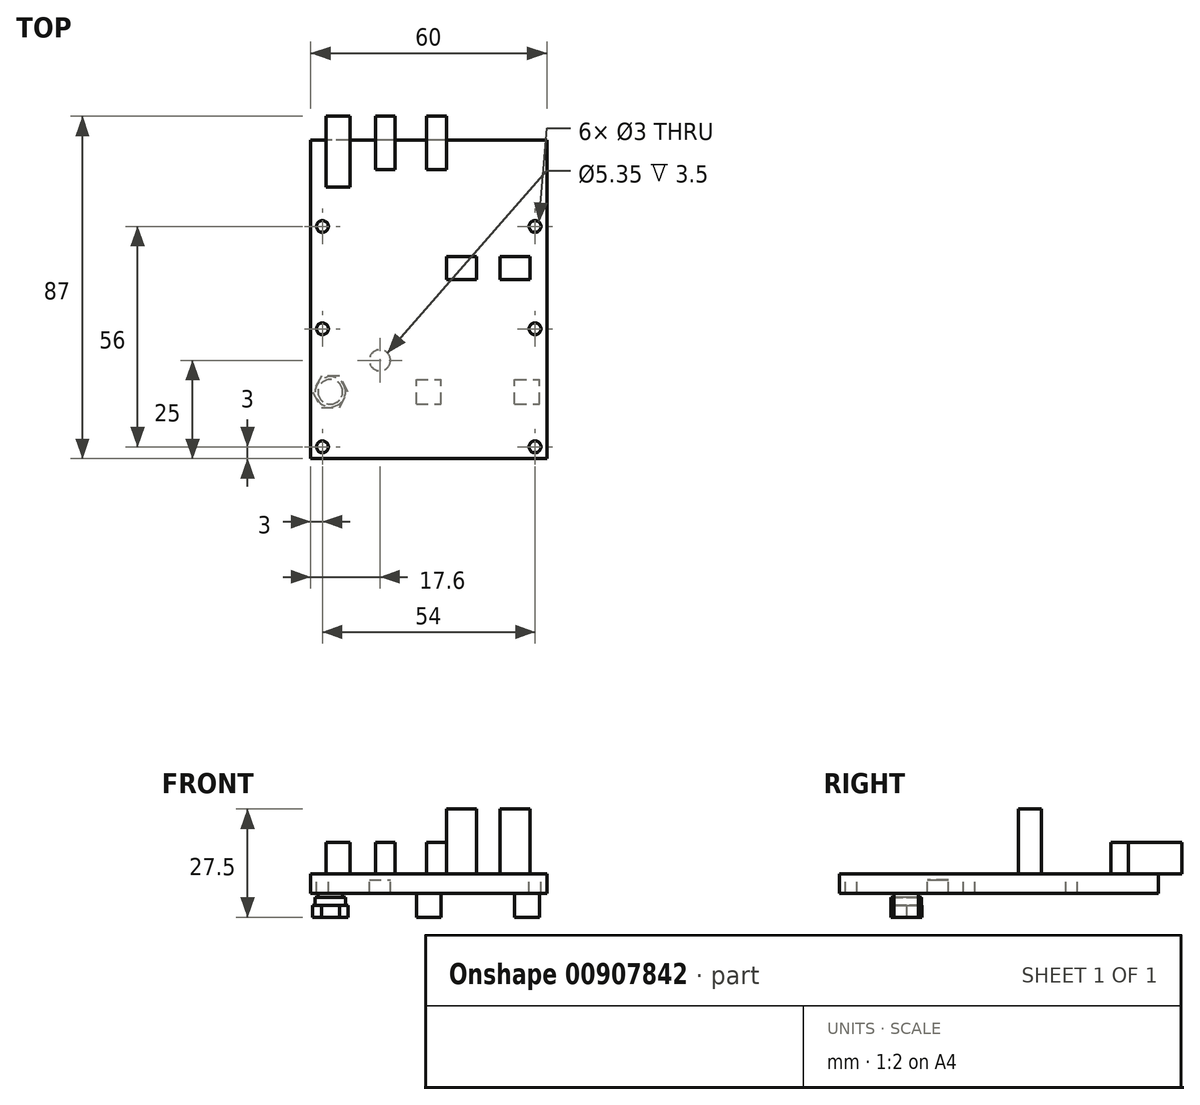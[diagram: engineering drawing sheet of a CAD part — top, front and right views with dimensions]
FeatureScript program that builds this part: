
annotation { "Feature Type Name" : "Feature", "Feature Type Description" : "" }
export const myFeature = defineFeature(function(context is Context, id is Id, definition is map)
    precondition{}
    {
        {
            var Q0;
            Q0=qCreatedBy(makeId("Top.planeOp"),FACE);
            var sketch = newSketch(context, id + "F0", { "sketchPlane" : qUnion([Q0])});
            skLineSegment(sketch, "E0.bottom", {"start": v(30, 40.5) * mm, "end": v(-30, 40.5) * mm});
            skLineSegment(sketch, "E0.top", {"start": v(30, -40.5) * mm, "end": v(-30, -40.5) * mm});
            skLineSegment(sketch, "E0.left", {"start": v(30, 40.5) * mm, "end": v(30, -40.5) * mm});
            skLineSegment(sketch, "E0.right", {"start": v(-30, 40.5) * mm, "end": v(-30, -40.5) * mm});
            skPoint(sketch, "E0.middle", {"position": v(0, 0) * mm});
            skSolve(sketch);
        }
        {
            var Q0;
            Q0=makeQuery(id+"F0.imprint","IMPRINT",FACE,{"disambiguationData":[TD([[makeQuery(id+"F0.imprint","IMPRINT",EDGE,{"derivedFrom":sQuery(id+"F0.wireOp",EDGE,"E0.bottom")}),1.0]])]});
            extrude(context, id + "F1", {"entities" : qUnion([Q0]), "depth" : 1.5 * mm, "offsetDistance" : 25 * mm});
        }
        {
            var Q0;
            Q0=makeQuery(id+"F1.opExtrude","CAP_FACE",FACE,{"disambiguationData":[OSD([sQuery(id+"F0.wireOp",EDGE,"E0.bottom"),sQuery(id+"F0.wireOp",EDGE,"E0.top"),sQuery(id+"F0.wireOp",EDGE,"E0.left"),sQuery(id+"F0.wireOp",EDGE,"E0.right")])],"isStart":false});
            var sketch = newSketch(context, id + "F2", { "sketchPlane" : qUnion([Q0])});
            skLineSegment(sketch, "E1", {"start": v(-27, -40.5) * mm, "end": v(-27, 40.5) * mm, "construction": true});
            skLineSegment(sketch, "E2", {"start": v(27, -40.5) * mm, "end": v(27, 40.5) * mm, "construction": true});
            skLineSegment(sketch, "E3", {"start": v(0, -40.5) * mm, "end": v(0, 40.5) * mm, "construction": true});
            skLineSegment(sketch, "E4", {"start": v(-30, -37.5) * mm, "end": v(30, -37.5) * mm, "construction": true});
            skLineSegment(sketch, "E5", {"start": v(-30, -7.5) * mm, "end": v(30, -7.5) * mm, "construction": true});
            skLineSegment(sketch, "E6", {"start": v(-30, 18.5) * mm, "end": v(30, 18.5) * mm, "construction": true});
            skCircle(sketch, "E7", {"center": v(-27, -37.5) * mm, "radius": 1.5 * mm});
            skCircle(sketch, "E8", {"center": v(-27, -7.5) * mm, "radius": 1.5 * mm});
            skCircle(sketch, "E9", {"center": v(-27, 18.5) * mm, "radius": 1.5 * mm});
            skCircle(sketch, "E10", {"center": v(27, 18.5) * mm, "radius": 1.5 * mm});
            skCircle(sketch, "E11", {"center": v(27, -7.5) * mm, "radius": 1.5 * mm});
            skCircle(sketch, "E12", {"center": v(27, -37.5) * mm, "radius": 1.5 * mm});
            skSolve(sketch);
        }
        {
            var Q0;
            Q0=makeQuery(id+"F2.imprint","IMPRINT",FACE,{"disambiguationData":[TD([[makeQuery(id+"F2.imprint","IMPRINT",EDGE,{"derivedFrom":sQuery(id+"F2.wireOp",EDGE,"E7")}),1.0]])]});
            var Q1;
            Q1=makeQuery(id+"F2.imprint","IMPRINT",FACE,{"disambiguationData":[TD([[makeQuery(id+"F2.imprint","IMPRINT",EDGE,{"derivedFrom":sQuery(id+"F2.wireOp",EDGE,"E8")}),1.0]])]});
            var Q2;
            Q2=makeQuery(id+"F2.imprint","IMPRINT",FACE,{"disambiguationData":[TD([[makeQuery(id+"F2.imprint","IMPRINT",EDGE,{"derivedFrom":sQuery(id+"F2.wireOp",EDGE,"E9")}),1.0]])]});
            var Q3;
            Q3=makeQuery(id+"F2.imprint","IMPRINT",FACE,{"disambiguationData":[TD([[makeQuery(id+"F2.imprint","IMPRINT",EDGE,{"derivedFrom":sQuery(id+"F2.wireOp",EDGE,"E10")}),1.0]])]});
            var Q4;
            Q4=makeQuery(id+"F2.imprint","IMPRINT",FACE,{"disambiguationData":[TD([[makeQuery(id+"F2.imprint","IMPRINT",EDGE,{"derivedFrom":sQuery(id+"F2.wireOp",EDGE,"E11")}),1.0]])]});
            var Q5;
            Q5=makeQuery(id+"F2.imprint","IMPRINT",FACE,{"disambiguationData":[TD([[makeQuery(id+"F2.imprint","IMPRINT",EDGE,{"derivedFrom":sQuery(id+"F2.wireOp",EDGE,"E12")}),1.0]])]});
            extrude(context, id + "F3", {"entities" : qUnion([Q0, Q1, Q2, Q3, Q4, Q5]), "operationType" : NewBodyOperationType.REMOVE, "endBound" : BoundingType.THROUGH_ALL, "oppositeDirection" : true, "depth" : 25 * mm, "offsetDistance" : 25 * mm});
        }
        {
            var Q0;
            Q0=makeQuery(id+"F1.opExtrude","CAP_FACE",FACE,{"disambiguationData":[OSD([sQuery(id+"F0.wireOp",EDGE,"E0.bottom"),sQuery(id+"F0.wireOp",EDGE,"E0.top"),sQuery(id+"F0.wireOp",EDGE,"E0.left"),sQuery(id+"F0.wireOp",EDGE,"E0.right")])],"isStart":false});
            var sketch = newSketch(context, id + "F4", { "sketchPlane" : qUnion([Q0])});
            skLineSegment(sketch, "E13.bottom", {"start": v(4.55, 10.8) * mm, "end": v(12.15, 10.8) * mm});
            skLineSegment(sketch, "E13.top", {"start": v(4.55, 5) * mm, "end": v(12.15, 5) * mm});
            skLineSegment(sketch, "E13.left", {"start": v(4.55, 10.8) * mm, "end": v(4.55, 5) * mm});
            skLineSegment(sketch, "E13.right", {"start": v(12.15, 10.8) * mm, "end": v(12.15, 5) * mm});
            skLineSegment(sketch, "E14.bottom", {"start": v(18.15, 10.8) * mm, "end": v(25.75, 10.8) * mm});
            skLineSegment(sketch, "E14.top", {"start": v(18.15, 5) * mm, "end": v(25.75, 5) * mm});
            skLineSegment(sketch, "E14.left", {"start": v(18.15, 10.8) * mm, "end": v(18.15, 5) * mm});
            skLineSegment(sketch, "E14.right", {"start": v(25.75, 10.8) * mm, "end": v(25.75, 5) * mm});
            skSolve(sketch);
        }
        {
            var Q0;
            Q0=makeQuery(id+"F4.imprint","IMPRINT",FACE,{"disambiguationData":[TD([[makeQuery(id+"F4.imprint","IMPRINT",EDGE,{"derivedFrom":sQuery(id+"F4.wireOp",EDGE,"E13.bottom")}),-1.0]])]});
            var Q1;
            Q1=makeQuery(id+"F4.imprint","IMPRINT",FACE,{"disambiguationData":[TD([[makeQuery(id+"F4.imprint","IMPRINT",EDGE,{"derivedFrom":sQuery(id+"F4.wireOp",EDGE,"E14.bottom")}),-1.0]])]});
            extrude(context, id + "F5", {"entities" : qUnion([Q0, Q1]), "operationType" : NewBodyOperationType.ADD, "depth" : 16.5 * mm, "offsetDistance" : 25 * mm});
        }
        {
            var Q0;
            Q0=makeQuery(id+"F1.opExtrude","CAP_FACE",FACE,{"disambiguationData":[OSD([sQuery(id+"F0.wireOp",EDGE,"E0.bottom"),sQuery(id+"F0.wireOp",EDGE,"E0.top"),sQuery(id+"F0.wireOp",EDGE,"E0.left"),sQuery(id+"F0.wireOp",EDGE,"E0.right")])],"isStart":false});
            var sketch = newSketch(context, id + "F6", { "sketchPlane" : qUnion([Q0])});
            skLineSegment(sketch, "E15.bottom", {"start": v(4.5, 32.9) * mm, "end": v(-0.5, 32.9) * mm});
            skLineSegment(sketch, "E15.top", {"start": v(4.5, 46.5) * mm, "end": v(-0.5, 46.5) * mm});
            skLineSegment(sketch, "E15.left", {"start": v(4.5, 32.9) * mm, "end": v(4.5, 46.5) * mm});
            skLineSegment(sketch, "E15.right", {"start": v(-0.5, 32.9) * mm, "end": v(-0.5, 46.5) * mm});
            skLineSegment(sketch, "E16.bottom", {"start": v(-8.5, 32.9) * mm, "end": v(-13.5, 32.9) * mm});
            skLineSegment(sketch, "E16.top", {"start": v(-8.5, 46.5) * mm, "end": v(-13.5, 46.5) * mm});
            skLineSegment(sketch, "E16.left", {"start": v(-8.5, 32.9) * mm, "end": v(-8.5, 46.5) * mm});
            skLineSegment(sketch, "E16.right", {"start": v(-13.5, 32.9) * mm, "end": v(-13.5, 46.5) * mm});
            skLineSegment(sketch, "E17.bottom", {"start": v(-19.97, 28.5) * mm, "end": v(-26.03, 28.5) * mm});
            skLineSegment(sketch, "E17.top", {"start": v(-19.98, 46.5) * mm, "end": v(-26.02, 46.5) * mm});
            skLineSegment(sketch, "E17.left", {"start": v(-19.98, 28.5) * mm, "end": v(-19.98, 46.5) * mm});
            skLineSegment(sketch, "E17.right", {"start": v(-26.03, 28.5) * mm, "end": v(-26.02, 46.5) * mm});
            skLineSegment(sketch, "E18", {"start": v(-23, 46.5) * mm, "end": v(-23, 28.5) * mm, "construction": true});
            skLineSegment(sketch, "E19", {"start": v(-11, 46.5) * mm, "end": v(-11, 32.9) * mm, "construction": true});
            skLineSegment(sketch, "E20", {"start": v(2, 46.5) * mm, "end": v(2, 32.9) * mm, "construction": true});
            skSolve(sketch);
        }
        {
            var Q0;
            Q0 = qSketchRegion(id + "F6", true);
            extrude(context, id + "F7", {"entities" : qUnion([Q0]), "operationType" : NewBodyOperationType.ADD, "depth" : 8 * mm, "offsetDistance" : 25 * mm});
        }
        {
            var Q0;
            Q0=makeQuery(id+"F1.opExtrude","CAP_FACE",FACE,{"disambiguationData":[OSD([sQuery(id+"F0.wireOp",EDGE,"E0.bottom"),sQuery(id+"F0.wireOp",EDGE,"E0.top"),sQuery(id+"F0.wireOp",EDGE,"E0.left"),sQuery(id+"F0.wireOp",EDGE,"E0.right")])],"isStart":true});
            var sketch = newSketch(context, id + "F8", { "sketchPlane" : qUnion([Q0])});
            skLineSegment(sketch, "E21.bottom", {"start": v(21.85, 26.65) * mm, "end": v(28.15, 26.65) * mm});
            skLineSegment(sketch, "E21.top", {"start": v(21.85, 20.35) * mm, "end": v(28.15, 20.35) * mm});
            skLineSegment(sketch, "E21.left", {"start": v(21.85, 26.65) * mm, "end": v(21.85, 20.35) * mm});
            skLineSegment(sketch, "E21.right", {"start": v(28.15, 26.65) * mm, "end": v(28.15, 20.35) * mm});
            skPoint(sketch, "E21.middle", {"position": v(25, 23.5) * mm});
            skLineSegment(sketch, "E22.bottom", {"start": v(-3.15, 26.65) * mm, "end": v(3.15, 26.65) * mm});
            skLineSegment(sketch, "E22.top", {"start": v(-3.15, 20.35) * mm, "end": v(3.15, 20.35) * mm});
            skLineSegment(sketch, "E22.left", {"start": v(-3.15, 26.65) * mm, "end": v(-3.15, 20.35) * mm});
            skLineSegment(sketch, "E22.right", {"start": v(3.15, 26.65) * mm, "end": v(3.15, 20.35) * mm});
            skPoint(sketch, "E22.middle", {"position": v(0, 23.5) * mm});
            skLineSegment(sketch, "E23.bottom", {"start": v(-28.15, 26.65) * mm, "end": v(-21.85, 26.65) * mm, "construction": true});
            skLineSegment(sketch, "E23.top", {"start": v(-28.15, 20.35) * mm, "end": v(-21.85, 20.35) * mm, "construction": true});
            skLineSegment(sketch, "E23.left", {"start": v(-28.15, 26.65) * mm, "end": v(-28.15, 20.35) * mm, "construction": true});
            skLineSegment(sketch, "E23.right", {"start": v(-21.85, 26.65) * mm, "end": v(-21.85, 20.35) * mm, "construction": true});
            skPoint(sketch, "E23.middle", {"position": v(-25, 23.5) * mm});
            skLineSegment(sketch, "E24", {"start": v(0, 40.5) * mm, "end": v(0, 23.5) * mm, "construction": true});
            skCircle(sketch, "E25", {"center": v(-25, 23.5) * mm, "radius": 3.15 * mm});
            skSolve(sketch);
        }
        {
            var Q0;
            Q0=makeQuery(id+"F8.imprint","IMPRINT",FACE,{"disambiguationData":[TD([[makeQuery(id+"F8.imprint","IMPRINT",EDGE,{"derivedFrom":sQuery(id+"F8.wireOp",EDGE,"E25")}),1.0]])]});
            var Q1;
            Q1=makeQuery(id+"F8.imprint","IMPRINT",FACE,{"disambiguationData":[TD([[makeQuery(id+"F8.imprint","IMPRINT",EDGE,{"derivedFrom":sQuery(id+"F8.wireOp",EDGE,"E22.bottom")}),-1.0]])]});
            var Q2;
            Q2=makeQuery(id+"F8.imprint","IMPRINT",FACE,{"disambiguationData":[TD([[makeQuery(id+"F8.imprint","IMPRINT",EDGE,{"derivedFrom":sQuery(id+"F8.wireOp",EDGE,"E21.bottom")}),-1.0]])]});
            extrude(context, id + "F9", {"entities" : qUnion([Q0, Q1, Q2]), "operationType" : NewBodyOperationType.ADD, "depth" : 9.5 * mm, "offsetDistance" : 25 * mm});
        }
        {
            var Q0;
            Q0=makeQuery(id+"F1.opExtrude","CAP_FACE",FACE,{"disambiguationData":[OSD([sQuery(id+"F0.wireOp",EDGE,"E0.bottom"),sQuery(id+"F0.wireOp",EDGE,"E0.top"),sQuery(id+"F0.wireOp",EDGE,"E0.left"),sQuery(id+"F0.wireOp",EDGE,"E0.right")])],"isStart":true});
            var sketch = newSketch(context, id + "F10", { "sketchPlane" : qUnion([Q0])});
            skLineSegment(sketch, "E26", {"start": v(0, 0) * mm, "end": v(0, 40.5) * mm, "construction": true});
            skCircle(sketch, "E27", {"center": v(12.4, 15.5) * mm, "radius": 2.67 * mm});
            skCircle(sketch, "E28.MirrorC", {"center": v(-12.4, 15.5) * mm, "radius": 2.67 * mm});
            skSolve(sketch);
        }
        {
            var Q0;
            Q0=makeQuery(id+"F10.imprint","IMPRINT",FACE,{"disambiguationData":[TD([[makeQuery(id+"F10.imprint","IMPRINT",EDGE,{"derivedFrom":sQuery(id+"F10.wireOp",EDGE,"E27")}),1.0]])]});
            var Q1;
            Q1=makeQuery(id+"F10.imprint","IMPRINT",FACE,{"disambiguationData":[TD([[makeQuery(id+"F10.imprint","IMPRINT",EDGE,{"derivedFrom":sQuery(id+"F10.wireOp",EDGE,"E28.MirrorC")}),-1.0]])]});
            extrude(context, id + "F11", {"entities" : qUnion([Q0, Q1]), "operationType" : NewBodyOperationType.ADD, "depth" : 3.5 * mm, "offsetDistance" : 25 * mm});
        }
        {
            var Q0;
            Q0=makeQuery(id+"F9.opExtrude","CAP_FACE",FACE,{"disambiguationData":[OSD([sQuery(id+"F8.wireOp",EDGE,"E25")])],"isStart":false});
            var sketch = newSketch(context, id + "F12", { "sketchPlane" : qUnion([Q0])});
            skCircle(sketch, "E29", {"center": v(-25, 23.5) * mm, "radius": 3.85 * mm});
            skSolve(sketch);
        }
        {
            var Q0;
            Q0=makeQuery(id+"F12.imprint","IMPRINT",FACE,{"disambiguationData":[TD([[makeQuery(id+"F12.imprint","IMPRINT",EDGE,{"derivedFrom":sQuery(id+"F12.wireOp",EDGE,"E29")}),1.0]])]});
            var Q1;
            Q1=makeQuery(id+"F12.imprint","IMPRINT",FACE,{"disambiguationData":[TD([[makeQuery(id+"F12.imprint","IMPRINT",EDGE,{"derivedFrom":makeQuery(id+"F9.opExtrude","CAP_EDGE",EDGE,{"disambiguationData":[OSD([sQuery(id+"F8.wireOp",EDGE,"E25")])],"isStart":false})}),1.0]])]});
            extrude(context, id + "F13", {"entities" : qUnion([Q0, Q1]), "operationType" : NewBodyOperationType.ADD, "oppositeDirection" : true, "depth" : 5 * mm, "offsetDistance" : 25 * mm});
        }
        {
            var Q0;
            Q0=makeQuery(id+"F13.boolean.opBoolean","MERGE",FACE,{"derivedFrom":[makeQuery(id+"F9.opExtrude","CAP_FACE",FACE,{"disambiguationData":[OSD([sQuery(id+"F8.wireOp",EDGE,"E25")])],"isStart":false}),makeQuery(id+"F13.opExtrude","CAP_FACE",FACE,{"disambiguationData":[OSD([sQuery(id+"F12.wireOp",EDGE,"E29")])],"isStart":true})]});
            var sketch = newSketch(context, id + "F14", { "sketchPlane" : qUnion([Q0])});
            skCircle(sketch, "E30.cCircle", {"center": v(-25, 23.5) * mm, "radius": 3.95 * mm, "construction": true});
            skLineSegment(sketch, "E30.0", {"start": v(-22.72, 19.55) * mm, "end": v(-27.28, 19.55) * mm});
            skLineSegment(sketch, "E30.1", {"start": v(-27.28, 19.55) * mm, "end": v(-29.56, 23.5) * mm});
            skLineSegment(sketch, "E30.2", {"start": v(-29.56, 23.5) * mm, "end": v(-27.28, 27.45) * mm});
            skLineSegment(sketch, "E30.3", {"start": v(-27.28, 27.45) * mm, "end": v(-22.72, 27.45) * mm});
            skLineSegment(sketch, "E30.4", {"start": v(-22.72, 27.45) * mm, "end": v(-20.44, 23.5) * mm});
            skLineSegment(sketch, "E30.5", {"start": v(-20.44, 23.5) * mm, "end": v(-22.72, 19.55) * mm});
            skPoint(sketch, "E30.0.midPoint", {"position": v(-25, 19.55) * mm});
            skLineSegment(sketch, "E31", {"start": v(-25, 23.5) * mm, "end": v(-25, 19.65) * mm, "construction": true});
            skSolve(sketch);
        }
        {
            var Q0;
            Q0=makeQuery(id+"F14.imprint","IMPRINT",FACE,{"disambiguationData":[TD([[makeQuery(id+"F14.imprint","IMPRINT",EDGE,{"derivedFrom":sQuery(id+"F14.wireOp",EDGE,"E30.0")}),-1.0]])]});
            var Q1;
            Q1=makeQuery(id+"F14.imprint","IMPRINT",FACE,{"disambiguationData":[TD([[makeQuery(id+"F14.imprint","IMPRINT",EDGE,{"derivedFrom":makeQuery(id+"F13.opExtrude","CAP_EDGE",EDGE,{"disambiguationData":[OSD([sQuery(id+"F12.wireOp",EDGE,"E29")])],"isStart":true})}),1.0]])]});
            extrude(context, id + "F15", {"entities" : qUnion([Q0, Q1]), "operationType" : NewBodyOperationType.ADD, "oppositeDirection" : true, "depth" : 3 * mm, "offsetDistance" : 25 * mm});
        }
    });
